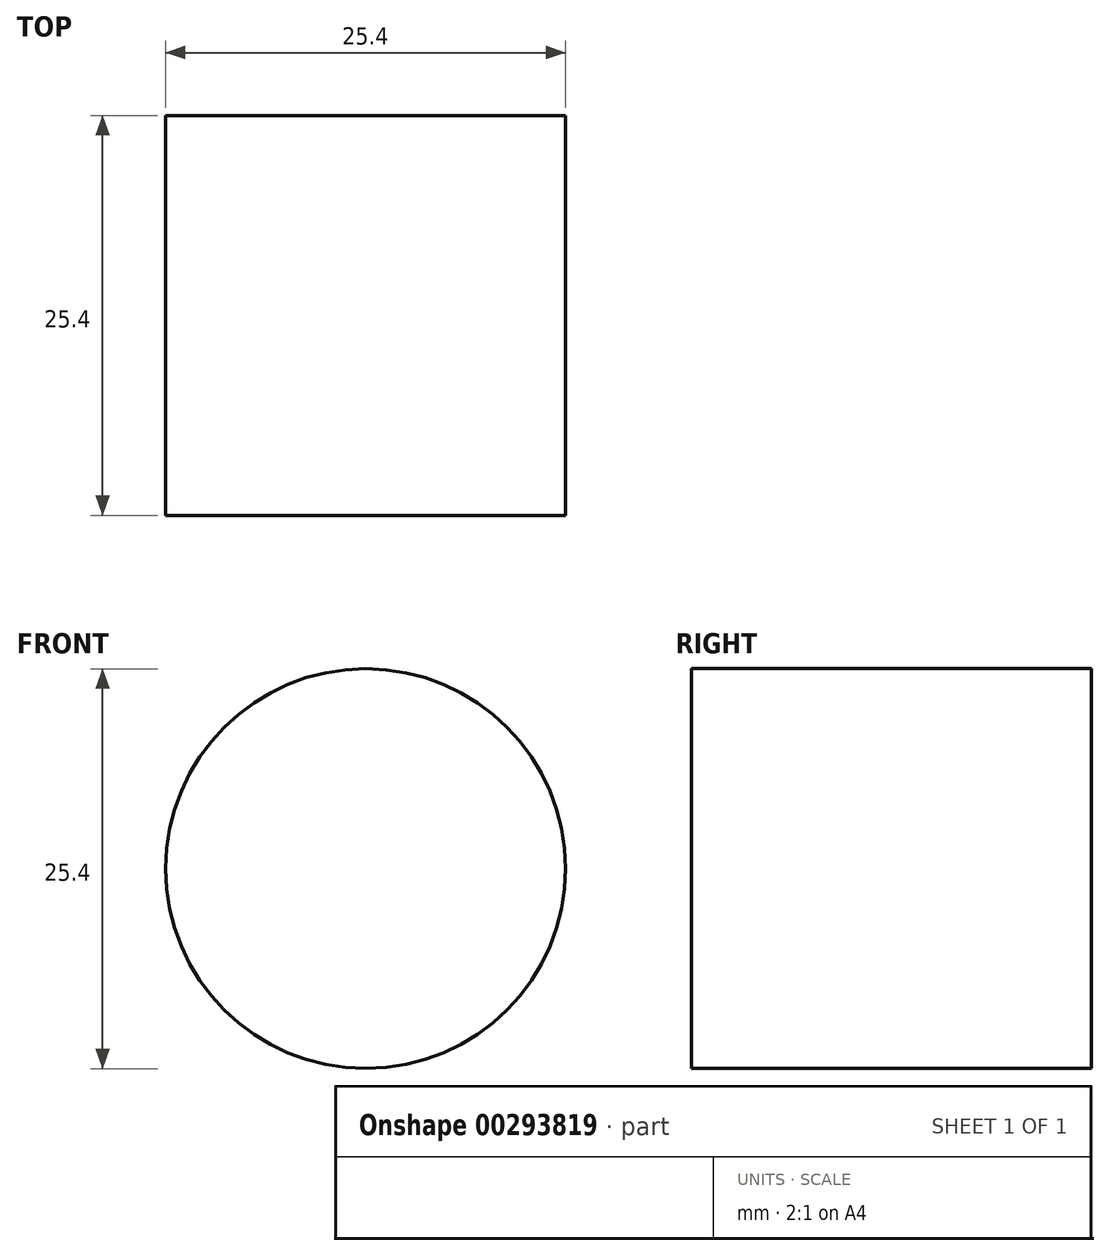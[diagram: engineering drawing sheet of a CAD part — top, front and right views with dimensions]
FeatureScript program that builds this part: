
annotation { "Feature Type Name" : "Feature", "Feature Type Description" : "" }
export const myFeature = defineFeature(function(context is Context, id is Id, definition is map)
    precondition{}
    {
        {
            var Q0;
            Q0=qCreatedBy(makeId("Front.planeOp"),FACE);
            var sketch = newSketch(context, id + "F0", { "sketchPlane" : qUnion([Q0])});
            skLineSegment(sketch, "E0.bottom", {"start": v(-27.22, 85.43) * mm, "end": v(23.58, 85.43) * mm});
            skLineSegment(sketch, "E0.top", {"start": v(-27.22, -41.57) * mm, "end": v(23.58, -41.57) * mm});
            skLineSegment(sketch, "E0.left", {"start": v(-27.22, 85.43) * mm, "end": v(-27.22, -41.57) * mm});
            skLineSegment(sketch, "E0.right", {"start": v(23.58, 85.43) * mm, "end": v(23.58, -41.57) * mm});
            skCircle(sketch, "E1", {"center": v(-0.8, 60.3) * mm, "radius": 12.7 * mm});
            skCircle(sketch, "E2", {"center": v(-0.47, 21.66) * mm, "radius": 12.7 * mm});
            skCircle(sketch, "E3", {"center": v(0.08, -15.57) * mm, "radius": 12.7 * mm});
            skSolve(sketch);
        }
        {
            var Q0;
            Q0=sQuery(id+"F0.wireOp",EDGE,"E1");
            extrude(context, id + "F1", {"bodyType" : ToolBodyType.SURFACE, "surfaceEntities" : qUnion([Q0]), "depth" : 25.4 * mm});
        }
    });
